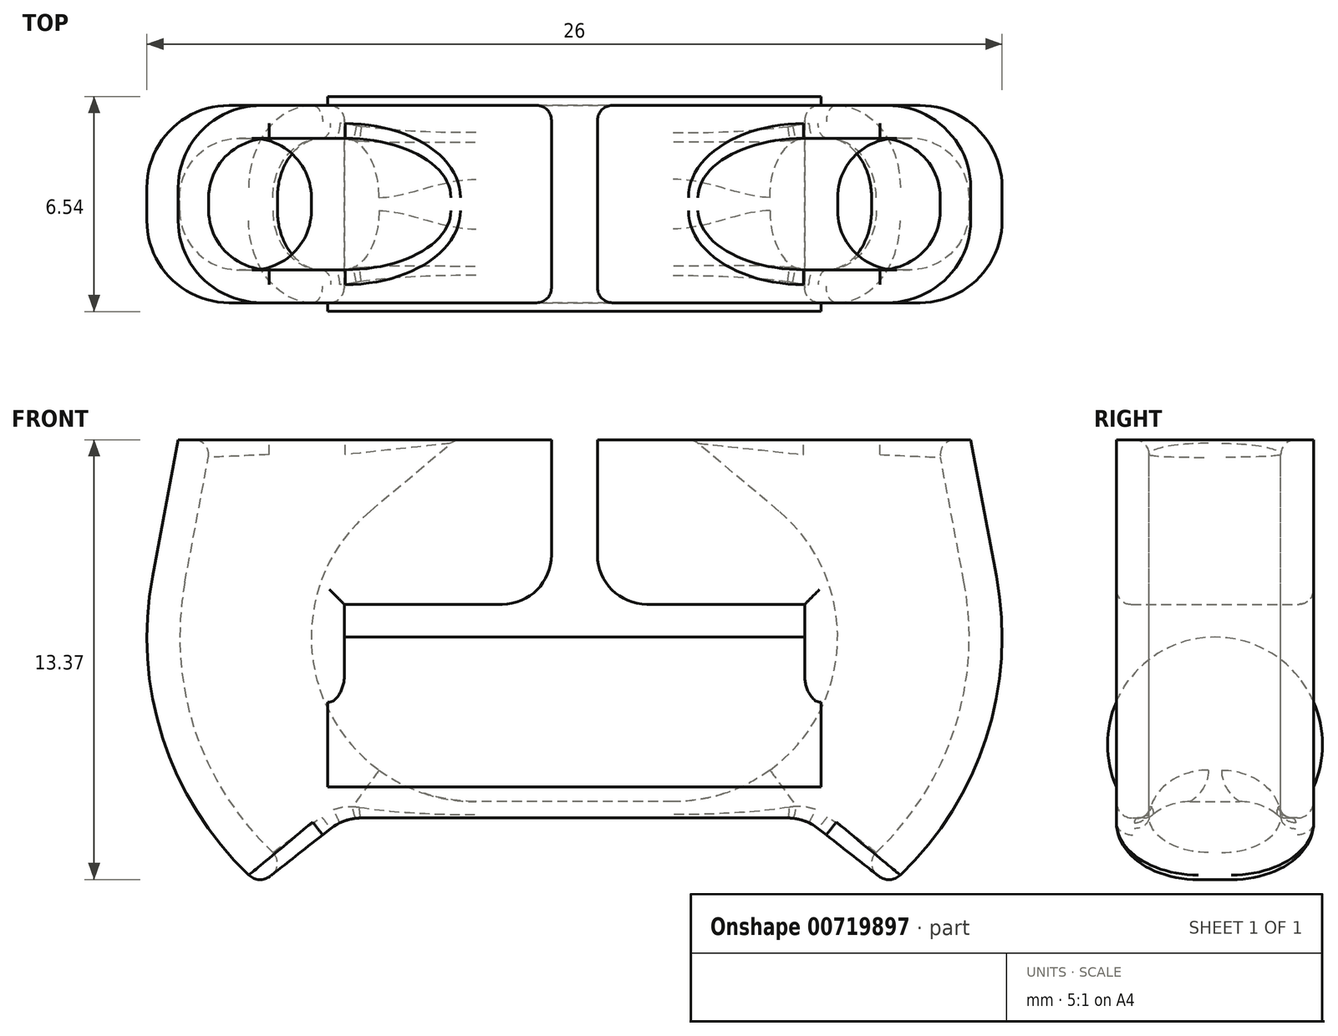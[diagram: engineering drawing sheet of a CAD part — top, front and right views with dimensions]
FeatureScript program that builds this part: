
annotation { "Feature Type Name" : "Feature", "Feature Type Description" : "" }
export const myFeature = defineFeature(function(context is Context, id is Id, definition is map)
    precondition{}
    {
        {
            var Q0;
            Q0=qCreatedBy(makeId("Front.planeOp"),FACE);
            var sketch = newSketch(context, id + "F0", { "sketchPlane" : qUnion([Q0])});
            skLineSegment(sketch, "E0.bottom", {"start": v(0, 0) * mm, "end": v(7, 0) * mm});
            skLineSegment(sketch, "E0.top", {"start": v(0, 1) * mm, "end": v(7, 1) * mm});
            skLineSegment(sketch, "E0.left", {"start": v(0, 0) * mm, "end": v(0, 1) * mm});
            skLineSegment(sketch, "E0.right", {"start": v(7, 0) * mm, "end": v(7, 1) * mm});
            skSolve(sketch);
        }
        {
            var Q0;
            Q0=qCreatedBy(makeId("Front.planeOp"),FACE);
            var sketch = newSketch(context, id + "F1", { "sketchPlane" : qUnion([Q0])});
            skArc(sketch, "E1", {"start": v(3, -10) * mm, "mid": v(10.7, -6.38) * mm, "end": v(12.83, 1.85) * mm});
            skLineSegment(sketch, "E2", {"start": v(12.83, 1.85) * mm, "end": v(12.05, 6) * mm});
            skLineSegment(sketch, "E3", {"start": v(12.05, 6) * mm, "end": v(0, 6) * mm});
            skLineSegment(sketch, "E4", {"start": v(0, 6) * mm, "end": v(0, -10) * mm});
            skPoint(sketch, "E5", {"position": v(13, 0) * mm});
            skPoint(sketch, "E6", {"position": v(0, 70) * mm});
            skLineSegment(sketch, "E7", {"start": v(0, -10) * mm, "end": v(3, -10) * mm});
            skSolve(sketch);
        }
        {
            var Q0;
            Q0=qSketchRegion(id+"F1",true);
            extrude(context, id + "F2", {"entities" : qUnion([Q0]), "depth" : 3 * mm, "offsetDistance" : 25 * mm});
        }
        {
            var Q0;
            Q0=qCreatedBy(makeId("Front.planeOp"),FACE);
            var sketch = newSketch(context, id + "F3", { "sketchPlane" : qUnion([Q0])});
            skArc(sketch, "E8", {"start": v(3, -5) * mm, "mid": v(7.7, -1.71) * mm, "end": v(6.21, 3.83) * mm});
            skArc(sketch, "E9.1", {"start": v(3, -9) * mm, "mid": v(9.93, -5.75) * mm, "end": v(11.84, 1.66) * mm});
            skLineSegment(sketch, "E10", {"start": v(11.84, 1.66) * mm, "end": v(11.03, 6) * mm});
            skLineSegment(sketch, "E11", {"start": v(6.21, 3.83) * mm, "end": v(3.63, 6) * mm});
            skPoint(sketch, "E12", {"position": v(8, 0) * mm});
            skPoint(sketch, "E13", {"position": v(12, 0) * mm});
            skLineSegment(sketch, "E14", {"start": v(3.63, 6) * mm, "end": v(11.03, 6) * mm});
            skLineSegment(sketch, "E15", {"start": v(3, -5) * mm, "end": v(0, -5) * mm});
            skLineSegment(sketch, "E16", {"start": v(0, -5) * mm, "end": v(0, -9) * mm});
            skLineSegment(sketch, "E17", {"start": v(0, -9) * mm, "end": v(3, -9) * mm});
            skSolve(sketch);
        }
        {
            var Q0;
            Q0=qSketchRegion(id+"F3",true);
            extrude(context, id + "F4", {"entities" : qUnion([Q0]), "operationType" : NewBodyOperationType.REMOVE, "depth" : 2 * mm, "offsetDistance" : 25 * mm});
        }
        {
            var Q0;
            Q0=qCreatedBy(makeId("Front.planeOp"),FACE);
            var sketch = newSketch(context, id + "F5", { "sketchPlane" : qUnion([Q0])});
            skLineSegment(sketch, "E18.0", {"start": v(0.7, 1) * mm, "end": v(7, 1) * mm});
            skPoint(sketch, "E19.0", {"position": v(7, 0) * mm});
            skLineSegment(sketch, "E20.0", {"start": v(7, 0) * mm, "end": v(7, 1) * mm});
            skLineSegment(sketch, "E21", {"start": v(0.7, 6) * mm, "end": v(0.7, 1) * mm});
            skLineSegment(sketch, "E22", {"start": v(0.7, 6) * mm, "end": v(0, 6) * mm});
            skLineSegment(sketch, "E23", {"start": v(0, 6) * mm, "end": v(0, 0) * mm});
            skPoint(sketch, "E24.orphan", {"position": v(0, 1) * mm});
            skLineSegment(sketch, "E25", {"start": v(7, 0) * mm, "end": v(7, -2) * mm});
            skLineSegment(sketch, "E26", {"start": v(7, -2) * mm, "end": v(0, -2) * mm});
            skLineSegment(sketch, "E27", {"start": v(0, -2) * mm, "end": v(0, 0) * mm});
            skSolve(sketch);
        }
        {
            var Q0;
            Q0=qSketchRegion(id+"F5",true);
            extrude(context, id + "F6", {"entities" : qUnion([Q0]), "operationType" : NewBodyOperationType.REMOVE, "endBound" : BoundingType.THROUGH_ALL, "depth" : 25 * mm, "offsetDistance" : 25 * mm});
        }
        {
            var Q0;
            Q0=qCreatedBy(makeId("Front.planeOp"),FACE);
            var sketch = newSketch(context, id + "F7", { "sketchPlane" : qUnion([Q0])});
            skArc(sketch, "E28", {"start": v(0, -15) * mm, "mid": v(6.56, -13.5) * mm, "end": v(11.8, -9.27) * mm});
            skLineSegment(sketch, "E29", {"start": v(11.8, -9.27) * mm, "end": v(7, -5.5) * mm});
            skLineSegment(sketch, "E30", {"start": v(0, -15) * mm, "end": v(0, -5.5) * mm});
            skLineSegment(sketch, "E31", {"start": v(7, -5.5) * mm, "end": v(0, -5.5) * mm});
            skSolve(sketch);
        }
        {
            var Q0;
            Q0=qSketchRegion(id+"F7",true);
            extrude(context, id + "F8", {"entities" : qUnion([Q0]), "operationType" : NewBodyOperationType.REMOVE, "endBound" : BoundingType.THROUGH_ALL, "depth" : 25 * mm, "offsetDistance" : 25 * mm});
        }
        {
            var Q0;
            Q0=qCreatedBy(makeId("Right.planeOp"),FACE);
            var sketch = newSketch(context, id + "F9", { "sketchPlane" : qUnion([Q0])});
            skCircle(sketch, "E32", {"center": v(0, -6.75) * mm, "radius": 1.75 * mm});
            skPoint(sketch, "E33", {"position": v(0, -5) * mm});
            skCircle(sketch, "E34", {"center": v(0, -3.27) * mm, "radius": 3.27 * mm});
            skLineSegment(sketch, "E35", {"start": v(0, -25) * mm, "end": v(-3.8, 0) * mm});
            skSolve(sketch);
        }
        {
            var Q0;
            Q0=qCreatedBy(makeId("Right.planeOp"),FACE);
            var sketch = newSketch(context, id + "F10", { "sketchPlane" : qUnion([Q0])});
            skPoint(sketch, "E36.orphan", {"position": v(-3.8, 0) * mm});
            skArc(sketch, "E37.0", {"start": v(0, 0) * mm, "mid": v(-2.89, -1.74) * mm, "end": v(-2.7, -5.1) * mm});
            skLineSegment(sketch, "E38", {"start": v(-2.7, -2.1) * mm, "end": v(-2.7, -5.1) * mm});
            skPoint(sketch, "E39.orphan", {"position": v(0, -25) * mm});
            skLineSegment(sketch, "E40", {"start": v(0, 0) * mm, "end": v(0, -2.1) * mm});
            skLineSegment(sketch, "E41", {"start": v(0, -2.1) * mm, "end": v(-2.7, -2.1) * mm});
            skSolve(sketch);
        }
        {
            var Q0;
            Q0=qSketchRegion(id+"F10",true);
            extrude(context, id + "F11", {"entities" : qUnion([Q0]), "operationType" : NewBodyOperationType.ADD, "depth" : 7.5 * mm, "offsetDistance" : 25 * mm});
        }
        {
            var Q0;
            Q0=makeQuery(id+"F2.opExtrude","CAP_EDGE",EDGE,{"disambiguationData":[OSD([sQuery(id+"F1.wireOp",EDGE,"E1")])],"isStart":false});
            fillet(context, id + "F12", {"entities" : qUnion([Q0]), "radius" : 2.5 * mm, "tangentPropagation" : true, "allowEdgeOverflow" : false});
        }
        {
            var Q0;
            Q0=makeQuery(id+"F4.boolean.opBoolean","COPY",EDGE,{"derivedFrom":makeQuery(id+"F4.opExtrude","CAP_EDGE",EDGE,{"disambiguationData":[OSD([sQuery(id+"F3.wireOp",EDGE,"E9.1")])],"isStart":false})});
            var Q1;
            Q1=makeQuery(id+"F4.boolean.opBoolean","COPY",EDGE,{"derivedFrom":makeQuery(id+"F4.opExtrude","CAP_EDGE",EDGE,{"disambiguationData":[OSD([sQuery(id+"F3.wireOp",EDGE,"E8")])],"isStart":false})});
            fillet(context, id + "F13", {"entities" : qUnion([Q0, Q1]), "radius" : 1.8 * mm, "tangentPropagation" : true, "allowEdgeOverflow" : false});
        }
        {
            var Q0;
            Q0=makeQuery(id+"F6.boolean.opBoolean","COPY",EDGE,{"derivedFrom":makeQuery(id+"F6.opExtrude","SWEPT_EDGE",EDGE,{"disambiguationData":[OSD([sQuery(id+"F5.wireOp",EDGE,"E18.0"),sQuery(id+"F5.wireOp",EDGE,"E21")])]})});
            var Q1;
            Q1=makeQuery(id+"F6.boolean.opBoolean","COPY",EDGE,{"derivedFrom":makeQuery(id+"F6.opExtrude","SWEPT_EDGE",EDGE,{"disambiguationData":[OSD([sQuery(id+"F5.wireOp",EDGE,"E21"),sQuery(id+"F5.wireOp",EDGE,"E22")])]})});
            var Q2;
            Q2=makeQuery(id+"F8.boolean.opBoolean","COPY",EDGE,{"derivedFrom":makeQuery(id+"F8.opExtrude","SWEPT_EDGE",EDGE,{"disambiguationData":[OSD([sQuery(id+"F7.wireOp",EDGE,"GExpFUsB-Pr3Z-94vW-ss1V-Dc07WEOKBbOR"),sQuery(id+"F7.wireOp",EDGE,"E29")])]})});
            fillet(context, id + "F14", {"entities" : qUnion([Q0, Q1, Q2]), "radius" : 1.5 * mm, "tangentPropagation" : true, "allowEdgeOverflow" : false});
        }
        {
            var Q0;
            Q0=makeQuery(id+"F6.boolean.opBoolean","INTERSECT",EDGE,{"derivedFrom":[makeQuery(id+"F2.opExtrude","CAP_FACE",FACE,{"disambiguationData":[OSD([sQuery(id+"F1.wireOp",EDGE,"E1"),sQuery(id+"F1.wireOp",EDGE,"E2"),sQuery(id+"F1.wireOp",EDGE,"E3"),sQuery(id+"F1.wireOp",EDGE,"E4")])],"isStart":false}),makeQuery(id+"F6.opExtrude","SWEPT_FACE",FACE,{"disambiguationData":[OSD([sQuery(id+"F5.wireOp",EDGE,"E18.0")])]})]});
            var Q1;
            Q1=makeQuery(id+"F11.boolean.opBoolean","SPLIT",EDGE,{"derivedFrom":makeQuery(id+"F6.boolean.opBoolean","INTERSECT",EDGE,{"derivedFrom":[makeQuery(id+"F2.opExtrude","CAP_FACE",FACE,{"disambiguationData":[OSD([sQuery(id+"F1.wireOp",EDGE,"E1"),sQuery(id+"F1.wireOp",EDGE,"E2"),sQuery(id+"F1.wireOp",EDGE,"E3"),sQuery(id+"F1.wireOp",EDGE,"E4")])],"isStart":false}),makeQuery(id+"F6.opExtrude","SWEPT_FACE",FACE,{"disambiguationData":[OSD([sQuery(id+"F5.wireOp",EDGE,"E20.0"),sQuery(id+"F5.wireOp",EDGE,"E25")])]})]})});
            var Q2;
            Q2=makeQuery(id+"F13.opFillet","BLEND_EDGE",EDGE,{"blendedFrom":[makeQuery(id+"F4.boolean.opBoolean","COPY",EDGE,{"derivedFrom":makeQuery(id+"F4.opExtrude","CAP_EDGE",EDGE,{"disambiguationData":[OSD([sQuery(id+"F3.wireOp",EDGE,"E10")])],"isStart":false})}),makeQuery(id+"F2.opExtrude","SWEPT_FACE",FACE,{"disambiguationData":[OSD([sQuery(id+"F1.wireOp",EDGE,"E3")])]})],"blendedInto":[makeQuery(id+"F2.opExtrude","SWEPT_FACE",FACE,{"disambiguationData":[OSD([sQuery(id+"F1.wireOp",EDGE,"E3")])]})]});
            var Q3;
            Q3=makeQuery(id+"F13.opFillet","BLEND_EDGE",EDGE,{"blendedFrom":[makeQuery(id+"F4.boolean.opBoolean","COPY",EDGE,{"derivedFrom":makeQuery(id+"F4.opExtrude","CAP_EDGE",EDGE,{"disambiguationData":[OSD([sQuery(id+"F3.wireOp",EDGE,"E8")])],"isStart":false})}),makeQuery(id+"F8.boolean.opBoolean","COPY",FACE,{"derivedFrom":makeQuery(id+"F8.opExtrude","SWEPT_FACE",FACE,{"disambiguationData":[OSD([sQuery(id+"F7.wireOp",EDGE,"E31")])]})})],"blendedInto":[makeQuery(id+"F8.boolean.opBoolean","COPY",FACE,{"derivedFrom":makeQuery(id+"F8.opExtrude","SWEPT_FACE",FACE,{"disambiguationData":[OSD([sQuery(id+"F7.wireOp",EDGE,"E31")])]})})]});
            var Q4;
            Q4=makeQuery(id+"F13.opFillet","BLEND_EDGE",EDGE,{"blendedFrom":[makeQuery(id+"F4.boolean.opBoolean","COPY",EDGE,{"derivedFrom":makeQuery(id+"F4.opExtrude","CAP_EDGE",EDGE,{"disambiguationData":[OSD([sQuery(id+"F3.wireOp",EDGE,"E9.1")])],"isStart":false})}),makeQuery(id+"F8.boolean.opBoolean","COPY",FACE,{"derivedFrom":makeQuery(id+"F8.opExtrude","SWEPT_FACE",FACE,{"disambiguationData":[OSD([sQuery(id+"F7.wireOp",EDGE,"E29")])]})})],"blendedInto":[makeQuery(id+"F8.boolean.opBoolean","COPY",FACE,{"derivedFrom":makeQuery(id+"F8.opExtrude","SWEPT_FACE",FACE,{"disambiguationData":[OSD([sQuery(id+"F7.wireOp",EDGE,"E29")])]})})]});
            fillet(context, id + "F15", {"entities" : qUnion([Q0, Q1, Q2, Q3, Q4]), "radius" : 0.45 * mm, "tangentPropagation" : true, "allowEdgeOverflow" : false});
        }
        {
            var Q0;
            Q0=makeQuery(id+"F8.boolean.opBoolean","INTERSECT",EDGE,{"derivedFrom":[makeQuery(id+"F2.opExtrude","CAP_FACE",FACE,{"disambiguationData":[OSD([sQuery(id+"F1.wireOp",EDGE,"E1"),sQuery(id+"F1.wireOp",EDGE,"E2"),sQuery(id+"F1.wireOp",EDGE,"E3"),sQuery(id+"F1.wireOp",EDGE,"E4")])],"isStart":false}),makeQuery(id+"F8.opExtrude","SWEPT_FACE",FACE,{"disambiguationData":[OSD([sQuery(id+"F7.wireOp",EDGE,"E31")])]})]});
            fillet(context, id + "F16", {"entities" : qUnion([Q0]), "radius" : 0.5 * mm, "tangentPropagation" : true, "allowEdgeOverflow" : false});
        }
        {
            var Q0;
            Q0=makeQuery(id+"F2.opExtrude","SWEPT_BODY",BODY,{"disambiguationData":[OSD([sQuery(id+"F1.wireOp",EDGE,"E1"),sQuery(id+"F1.wireOp",EDGE,"E2"),sQuery(id+"F1.wireOp",EDGE,"E3"),sQuery(id+"F1.wireOp",EDGE,"E4")])]});
            var Q1;
            Q1=qCreatedBy(makeId("Front.planeOp"),FACE);
            mirror(context, id + "F17", {"operationType" : NewBodyOperationType.ADD, "entities" : qUnion([Q0]), "mirrorPlane" : qUnion([Q1])});
        }
        {
            var Q0;
            Q0=makeQuery(id+"F2.opExtrude","SWEPT_BODY",BODY,{"disambiguationData":[OSD([sQuery(id+"F1.wireOp",EDGE,"E1"),sQuery(id+"F1.wireOp",EDGE,"E2"),sQuery(id+"F1.wireOp",EDGE,"E3"),sQuery(id+"F1.wireOp",EDGE,"E4")])]});
            var Q1;
            Q1=qCreatedBy(makeId("Right.planeOp"),FACE);
            mirror(context, id + "F18", {"operationType" : NewBodyOperationType.ADD, "entities" : qUnion([Q0]), "mirrorPlane" : qUnion([Q1])});
        }
    });
